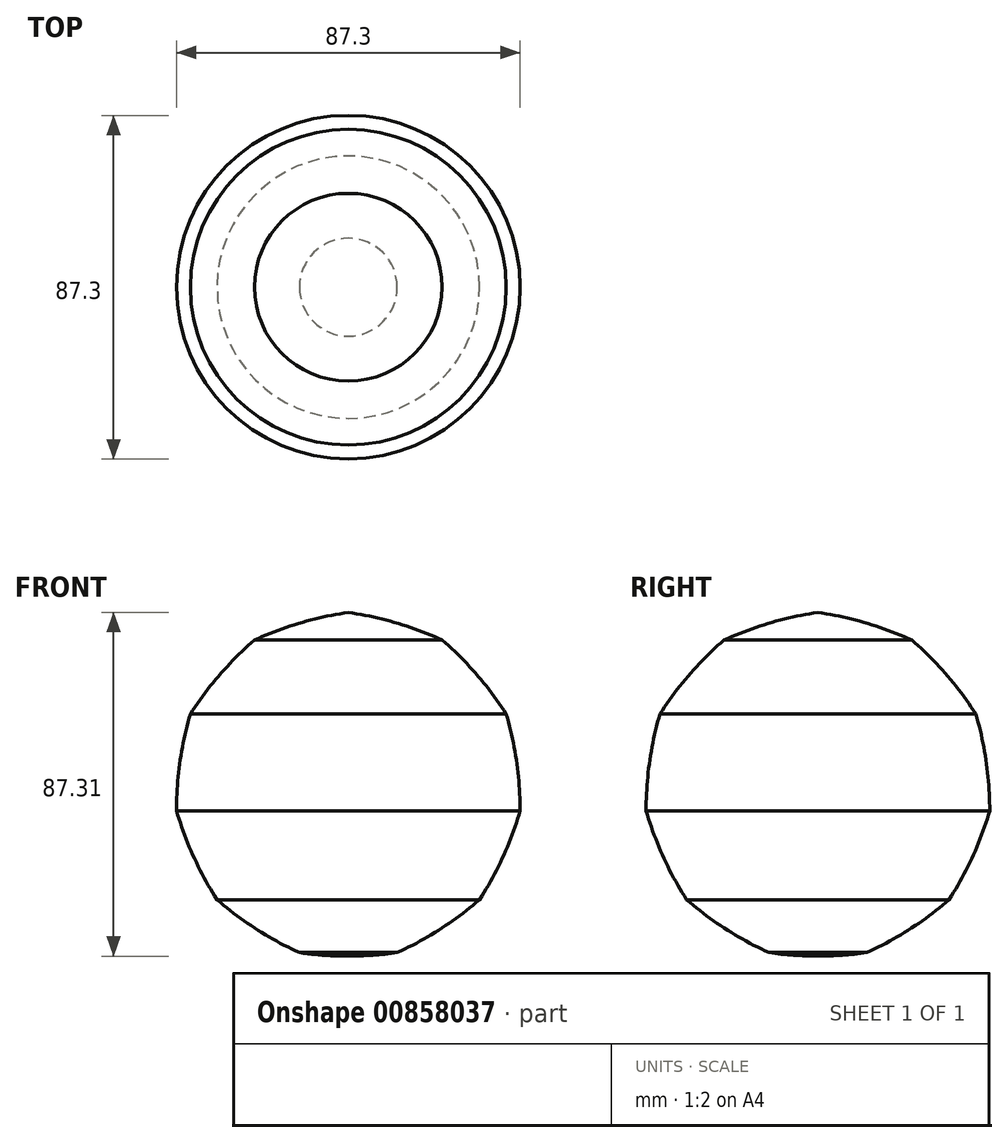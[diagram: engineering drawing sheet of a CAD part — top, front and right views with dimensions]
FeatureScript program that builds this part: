
annotation { "Feature Type Name" : "Feature", "Feature Type Description" : "" }
export const myFeature = defineFeature(function(context is Context, id is Id, definition is map)
    precondition{}
    {
        {
            var Q0;
            Q0=qCreatedBy(makeId("Front.planeOp"),FACE);
            var sketch = newSketch(context, id + "F0", { "sketchPlane" : qUnion([Q0])});
            skPoint(sketch, "E0.0.midPoint", {"position": v(0, -43.2) * mm});
            skCircle(sketch, "E1", {"center": v(-23.84, 37.1) * mm, "radius": 87.3 * mm});
            skCircle(sketch, "E2", {"center": v(0, 44.1) * mm, "radius": 87.3 * mm});
            skCircle(sketch, "E3", {"center": v(23.84, 37.1) * mm, "radius": 87.3 * mm});
            skCircle(sketch, "E4", {"center": v(40.12, 18.32) * mm, "radius": 87.3 * mm});
            skCircle(sketch, "E5", {"center": v(43.65, -6.28) * mm, "radius": 87.3 * mm});
            skCircle(sketch, "E6", {"center": v(33.33, -28.88) * mm, "radius": 87.3 * mm});
            skCircle(sketch, "E7", {"center": v(14.48, -42) * mm, "radius": 87.3 * mm});
            skCircle(sketch, "E8", {"center": v(-12.43, -42.32) * mm, "radius": 87.3 * mm});
            skCircle(sketch, "E9", {"center": v(-33.33, -28.88) * mm, "radius": 87.3 * mm});
            skCircle(sketch, "E10", {"center": v(-43.65, -6.28) * mm, "radius": 87.3 * mm});
            skCircle(sketch, "E11", {"center": v(-40.12, 18.32) * mm, "radius": 87.3 * mm});
            skLineSegment(sketch, "E12", {"start": v(0, 44.1) * mm, "end": v(0, -43.2) * mm});
            skSolve(sketch);
        }
        {
            var Q0;
            {var subQ0=sQuery(id+"F0.wireOp",EDGE,"E12");Q0=makeQuery(id+"F0.imprint","IMPRINT",FACE,{"disambiguationData":[TD([[makeQuery(id+"F0.imprint","IMPRINT",EDGE,{"derivedFrom":subQ0}),1.0]])]});}
            var Q1;
            Q1=sQuery(id+"F0.wireOp",EDGE,"E12");
            revolve(context, id + "F1", {"surfaceOperationType" : NewSurfaceOperationType.NEW, "entities" : qUnion([Q0]), "axis" : qUnion([Q1]), "revolveType" : RevolveType.FULL});
        }
    });
